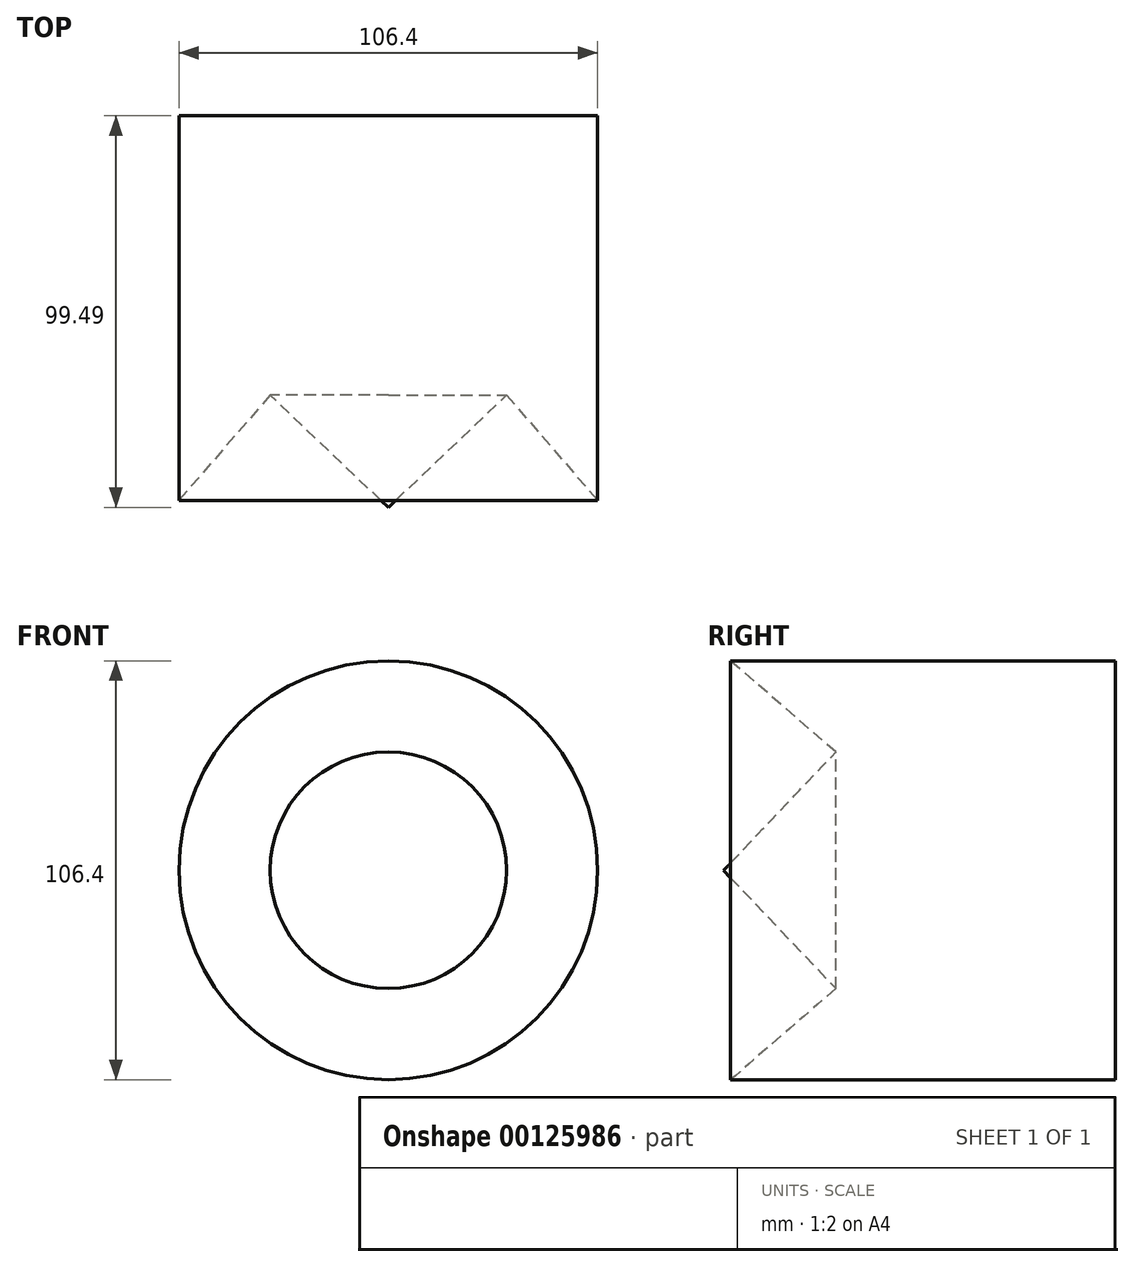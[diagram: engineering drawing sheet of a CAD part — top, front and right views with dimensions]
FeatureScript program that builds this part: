
annotation { "Feature Type Name" : "Feature", "Feature Type Description" : "" }
export const myFeature = defineFeature(function(context is Context, id is Id, definition is map)
    precondition{}
    {
        {
            var Q0;
            Q0=qCreatedBy(makeId("Top.planeOp"),FACE);
            var sketch = newSketch(context, id + "F0", { "sketchPlane" : qUnion([Q0])});
            skLineSegment(sketch, "E0", {"start": v(0, 48.73) * mm, "end": v(-53.2, 48.73) * mm});
            skLineSegment(sketch, "E1", {"start": v(-53.2, 48.73) * mm, "end": v(-53.2, -48.98) * mm});
            skLineSegment(sketch, "E2", {"start": v(-53.2, -48.98) * mm, "end": v(-30.04, -22.26) * mm});
            skLineSegment(sketch, "E3", {"start": v(-30.04, -22.26) * mm, "end": v(0, -50.76) * mm});
            skLineSegment(sketch, "E4", {"start": v(0, -50.76) * mm, "end": v(0, 48.73) * mm});
            skSolve(sketch);
        }
        {
            var Q0;
            Q0=makeQuery(id+"F0.imprint","IMPRINT",FACE,{"disambiguationData":[TD([[makeQuery(id+"F0.imprint","IMPRINT",EDGE,{"derivedFrom":sQuery(id+"F0.wireOp",EDGE,"E0")}),1.0]])]});
            var Q1;
            Q1=sQuery(id+"F0.wireOp",EDGE,"E4");
            revolve(context, id + "F1", {"entities" : qUnion([Q0]), "axis" : qUnion([Q1]), "revolveType" : RevolveType.FULL});
        }
    });
